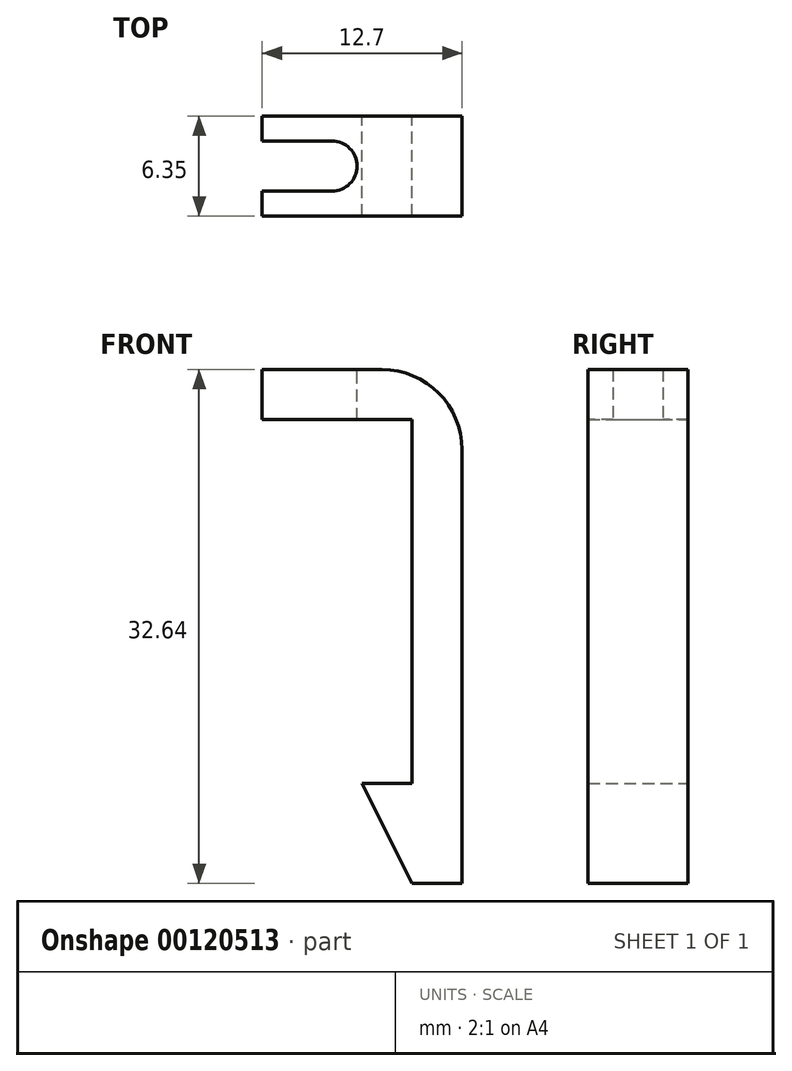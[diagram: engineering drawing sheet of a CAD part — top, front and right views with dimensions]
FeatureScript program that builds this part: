
annotation { "Feature Type Name" : "Feature", "Feature Type Description" : "" }
export const myFeature = defineFeature(function(context is Context, id is Id, definition is map)
    precondition{}
    {
        {
            var Q0;
            Q0=qCreatedBy(makeId("Front.planeOp"),FACE);
            var sketch = newSketch(context, id + "F0", { "sketchPlane" : qUnion([Q0])});
            skLineSegment(sketch, "E0.bottom", {"start": v(0, 0) * mm, "end": v(20.96, 0) * mm});
            skLineSegment(sketch, "E0.top", {"start": v(0, 3.17) * mm, "end": v(20.96, 3.17) * mm});
            skLineSegment(sketch, "E0.left", {"start": v(0, 0) * mm, "end": v(0, 3.17) * mm});
            skLineSegment(sketch, "E0.right", {"start": v(20.96, 0) * mm, "end": v(20.96, 3.17) * mm});
            skLineSegment(sketch, "E1.bottom", {"start": v(20.96, 0) * mm, "end": v(17.78, 0) * mm});
            skLineSegment(sketch, "E1.top", {"start": v(20.96, -29.46) * mm, "end": v(17.78, -29.46) * mm});
            skLineSegment(sketch, "E1.left", {"start": v(20.96, 0) * mm, "end": v(20.96, -29.46) * mm});
            skLineSegment(sketch, "E1.right", {"start": v(17.78, 0) * mm, "end": v(17.78, -29.46) * mm});
            skLineSegment(sketch, "E2", {"start": v(17.78, -29.46) * mm, "end": v(14.6, -23.11) * mm});
            skLineSegment(sketch, "E3", {"start": v(14.6, -23.11) * mm, "end": v(17.78, -23.11) * mm});
            skLineSegment(sketch, "E4", {"start": v(17.78, -23.11) * mm, "end": v(17.78, -29.46) * mm});
            skSolve(sketch);
        }
        {
            var Q0;
            Q0 = qSketchRegion(id + "F0", true);
            extrude(context, id + "F1", {"entities" : qUnion([Q0]), "depth" : 6.35 * mm});
        }
        {
            var Q0;
            Q0=makeQuery(id+"F1.opExtrude","SWEPT_EDGE",EDGE,{"disambiguationData":[OSD([sQuery(id+"F0.wireOp",EDGE,"E0.top"),sQuery(id+"F0.wireOp",EDGE,"E0.right")])]});
            fillet(context, id + "F2", {"entities" : qUnion([Q0]), "radius" : 5.08 * mm, "tangentPropagation" : true, "allowEdgeOverflow" : false});
        }
        {
            var Q0;
            Q0=makeQuery(id+"F1.opExtrude","SWEPT_FACE",FACE,{"disambiguationData":[OSD([sQuery(id+"F0.wireOp",EDGE,"E0.top")])]});
            var sketch = newSketch(context, id + "F3", { "sketchPlane" : qUnion([Q0])});
            skLineSegment(sketch, "E5.bottom", {"start": v(2.54, -4.76) * mm, "end": v(12.7, -4.76) * mm});
            skLineSegment(sketch, "E5.top", {"start": v(2.54, -1.59) * mm, "end": v(12.7, -1.59) * mm});
            skLineSegment(sketch, "E5.left", {"start": v(2.54, -4.76) * mm, "end": v(2.54, -1.59) * mm});
            skLineSegment(sketch, "E5.right", {"start": v(12.7, -4.76) * mm, "end": v(12.7, -1.59) * mm});
            skCircle(sketch, "E6", {"center": v(2.54, -3.18) * mm, "radius": 1.59 * mm});
            skCircle(sketch, "E7", {"center": v(12.7, -3.17) * mm, "radius": 1.59 * mm});
            skSolve(sketch);
        }
        {
            var Q0;
            Q0 = qSketchRegion(id + "F3", true);
            extrude(context, id + "F4", {"entities" : qUnion([Q0]), "operationType" : NewBodyOperationType.REMOVE, "oppositeDirection" : true, "depth" : 25.4 * mm});
        }
        {
            var Q0;
            Q0=makeQuery(id+"F1.opExtrude","SWEPT_FACE",FACE,{"disambiguationData":[OSD([sQuery(id+"F0.wireOp",EDGE,"E0.top")])]});
            var sketch = newSketch(context, id + "F5", { "sketchPlane" : qUnion([Q0])});
            skLineSegment(sketch, "E8.bottom", {"start": v(0, 0) * mm, "end": v(8.26, 0) * mm});
            skLineSegment(sketch, "E8.top", {"start": v(0, -6.35) * mm, "end": v(8.26, -6.35) * mm});
            skLineSegment(sketch, "E8.left", {"start": v(0, 0) * mm, "end": v(0, -6.35) * mm});
            skLineSegment(sketch, "E8.right", {"start": v(8.26, 0) * mm, "end": v(8.26, -6.35) * mm});
            skSolve(sketch);
        }
        {
            var Q0;
            Q0 = qSketchRegion(id + "F5", true);
            extrude(context, id + "F6", {"entities" : qUnion([Q0]), "operationType" : NewBodyOperationType.REMOVE, "oppositeDirection" : true, "depth" : 5 * mm});
        }
    });
